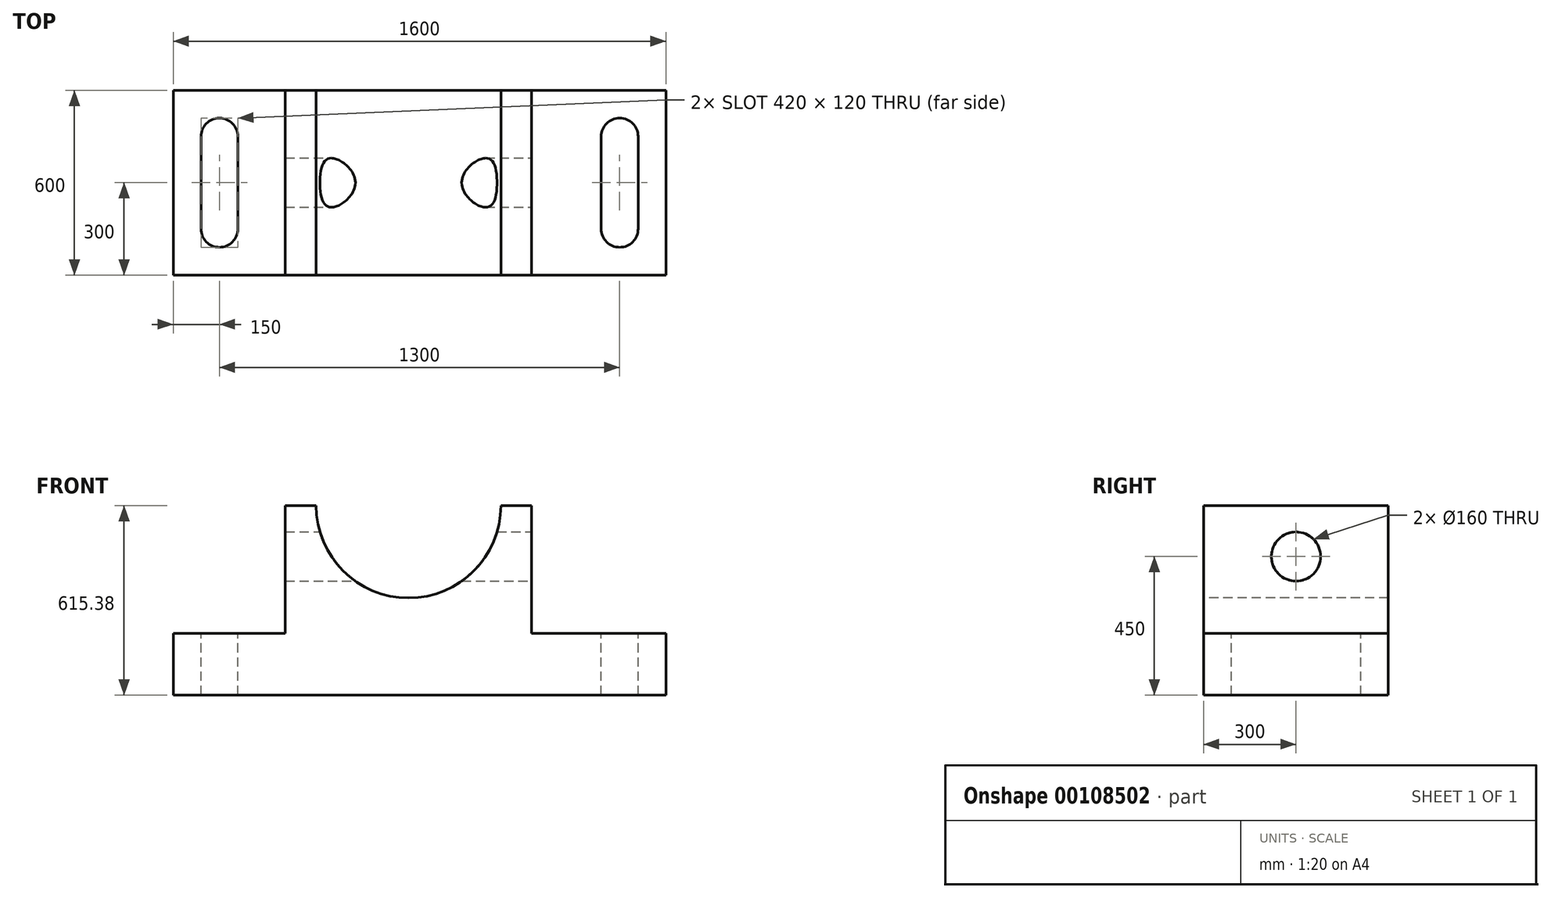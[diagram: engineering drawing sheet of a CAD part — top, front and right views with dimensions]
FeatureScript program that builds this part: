
annotation { "Feature Type Name" : "Feature", "Feature Type Description" : "" }
export const myFeature = defineFeature(function(context is Context, id is Id, definition is map)
    precondition{}
    {
        {
            var Q0;
            Q0=qCreatedBy(makeId("Front.planeOp"),FACE);
            var sketch = newSketch(context, id + "F0", { "sketchPlane" : qUnion([Q0])});
            skLineSegment(sketch, "E0", {"start": v(0, 0) * mm, "end": v(800, 0) * mm});
            skLineSegment(sketch, "E1", {"start": v(800, 0) * mm, "end": v(800, 200) * mm});
            skLineSegment(sketch, "E2", {"start": v(800, 200) * mm, "end": v(364.1, 200) * mm});
            skLineSegment(sketch, "E3", {"start": v(364.1, 200) * mm, "end": v(364.1, 615.38) * mm});
            skLineSegment(sketch, "E4", {"start": v(364.1, 615.38) * mm, "end": v(-435.9, 615.38) * mm});
            skLineSegment(sketch, "E5", {"start": v(-435.9, 615.38) * mm, "end": v(-435.9, 200) * mm});
            skLineSegment(sketch, "E6", {"start": v(-435.9, 200) * mm, "end": v(-800, 200) * mm});
            skLineSegment(sketch, "E7", {"start": v(-800, 200) * mm, "end": v(-800, 0) * mm});
            skLineSegment(sketch, "E8", {"start": v(-800, 0) * mm, "end": v(0, 0) * mm});
            skSolve(sketch);
        }
        {
            var Q0;
            Q0=makeQuery(id+"F0.imprint","IMPRINT",FACE,{"disambiguationData":[TD([[makeQuery(id+"F0.imprint","IMPRINT",EDGE,{"derivedFrom":sQuery(id+"F0.wireOp",EDGE,"E0")}),1.0]])]});
            extrude(context, id + "F1", {"entities" : qUnion([Q0]), "depth" : 600 * mm});
        }
        {
            var Q0;
            Q0=makeQuery(id+"F1.opExtrude","CAP_FACE",FACE,{"disambiguationData":[OSD([sQuery(id+"F0.wireOp",EDGE,"E0"),sQuery(id+"F0.wireOp",EDGE,"E1"),sQuery(id+"F0.wireOp",EDGE,"E2"),sQuery(id+"F0.wireOp",EDGE,"E3"),sQuery(id+"F0.wireOp",EDGE,"E4"),sQuery(id+"F0.wireOp",EDGE,"E5"),sQuery(id+"F0.wireOp",EDGE,"E6"),sQuery(id+"F0.wireOp",EDGE,"E7"),sQuery(id+"F0.wireOp",EDGE,"E8")])],"isStart":false});
            var sketch = newSketch(context, id + "F2", { "sketchPlane" : qUnion([Q0])});
            skPoint(sketch, "E9", {"position": v(-35.9, 615.38) * mm});
            skArc(sketch, "E10", {"start": v(-335.9, 615.38) * mm, "mid": v(-35.9, 315.38) * mm, "end": v(264.1, 615.38) * mm});
            skSolve(sketch);
        }
        {
            var Q0;
            Q0 = qSketchRegion(id + "F2", true);
            var Q1;
            {var subQ0=sQuery(id+"F2.wireOp",EDGE,"E10");Q1=makeQuery(id+"F2.imprint","IMPRINT",FACE,{"disambiguationData":[TD([[makeQuery(id+"F2.imprint","IMPRINT",EDGE,{"derivedFrom":subQ0}),1.0]])]});}
            extrude(context, id + "F3", {"entities" : qUnion([Q0, Q1]), "operationType" : NewBodyOperationType.REMOVE, "endBound" : BoundingType.THROUGH_ALL, "oppositeDirection" : true, "depth" : 25 * mm});
        }
        {
            var Q0;
            Q0=makeQuery(id+"F1.opExtrude","SWEPT_FACE",FACE,{"disambiguationData":[OSD([sQuery(id+"F0.wireOp",EDGE,"E1")])]});
            var sketch = newSketch(context, id + "F4", { "sketchPlane" : qUnion([Q0])});
            skCircle(sketch, "E11", {"center": v(-300, 450) * mm, "radius": 80 * mm});
            skPoint(sketch, "E12.start.orphan", {"position": v(-300, 0) * mm});
            skSolve(sketch);
        }
        {
            var Q0;
            Q0=makeQuery(id+"F4.imprint","IMPRINT",FACE,{"disambiguationData":[TD([[makeQuery(id+"F4.imprint","IMPRINT",EDGE,{"derivedFrom":sQuery(id+"F4.wireOp",EDGE,"E11")}),1.0]])]});
            extrude(context, id + "F5", {"entities" : qUnion([Q0]), "operationType" : NewBodyOperationType.REMOVE, "endBound" : BoundingType.THROUGH_ALL, "oppositeDirection" : true, "depth" : 25 * mm});
        }
        {
            var Q0;
            Q0=makeQuery(id+"F1.opExtrude","SWEPT_FACE",FACE,{"disambiguationData":[OSD([sQuery(id+"F0.wireOp",EDGE,"E2")])]});
            var sketch = newSketch(context, id + "F6", { "sketchPlane" : qUnion([Q0])});
            skLineSegment(sketch, "E13.left", {"start": v(-710, -450) * mm, "end": v(-710, -150) * mm});
            skLineSegment(sketch, "E13.right", {"start": v(-590, -450) * mm, "end": v(-590, -150) * mm});
            skPoint(sketch, "E13.middle", {"position": v(-650, -300) * mm});
            skPoint(sketch, "E13.middle.positionSnap0", {"position": v(-800, -300) * mm});
            skPoint(sketch, "E13.centerSnap0", {"position": v(-800, -300) * mm});
            skLineSegment(sketch, "E14.left", {"start": v(590, -450) * mm, "end": v(590, -150) * mm});
            skLineSegment(sketch, "E14.right", {"start": v(710, -450) * mm, "end": v(710, -150) * mm});
            skPoint(sketch, "E14.middle", {"position": v(650, -300) * mm});
            skPoint(sketch, "E14.middle.positionSnap0", {"position": v(800, -300) * mm});
            skPoint(sketch, "E14.centerSnap0", {"position": v(800, -300) * mm});
            skArc(sketch, "E15", {"start": v(-590, -150) * mm, "mid": v(-650, -90) * mm, "end": v(-710, -150) * mm});
            skArc(sketch, "E16", {"start": v(-710, -450) * mm, "mid": v(-650, -510) * mm, "end": v(-590, -450) * mm});
            skArc(sketch, "E17", {"start": v(590, -450) * mm, "mid": v(650, -510) * mm, "end": v(710, -450) * mm});
            skArc(sketch, "E18", {"start": v(710, -150) * mm, "mid": v(650, -90) * mm, "end": v(590, -150) * mm});
            skSolve(sketch);
        }
        {
            var Q0;
            Q0=makeQuery(id+"F6.imprint","IMPRINT",FACE,{"disambiguationData":[TD([[makeQuery(id+"F6.imprint","IMPRINT",EDGE,{"derivedFrom":sQuery(id+"F6.wireOp",EDGE,"E13.left")}),-1.0]])]});
            var Q1;
            Q1=makeQuery(id+"F6.imprint","IMPRINT",FACE,{"disambiguationData":[TD([[makeQuery(id+"F6.imprint","IMPRINT",EDGE,{"derivedFrom":sQuery(id+"F6.wireOp",EDGE,"E13.left")}),-1.0]])]});
            var Q2;
            Q2=makeQuery(id+"F6.imprint","IMPRINT",FACE,{"disambiguationData":[TD([[makeQuery(id+"F6.imprint","IMPRINT",EDGE,{"derivedFrom":sQuery(id+"F6.wireOp",EDGE,"E14.left")}),-1.0]])]});
            extrude(context, id + "F7", {"entities" : qUnion([Q0, Q1, Q2]), "operationType" : NewBodyOperationType.REMOVE, "endBound" : BoundingType.THROUGH_ALL, "oppositeDirection" : true, "depth" : 25 * mm});
        }
    });
